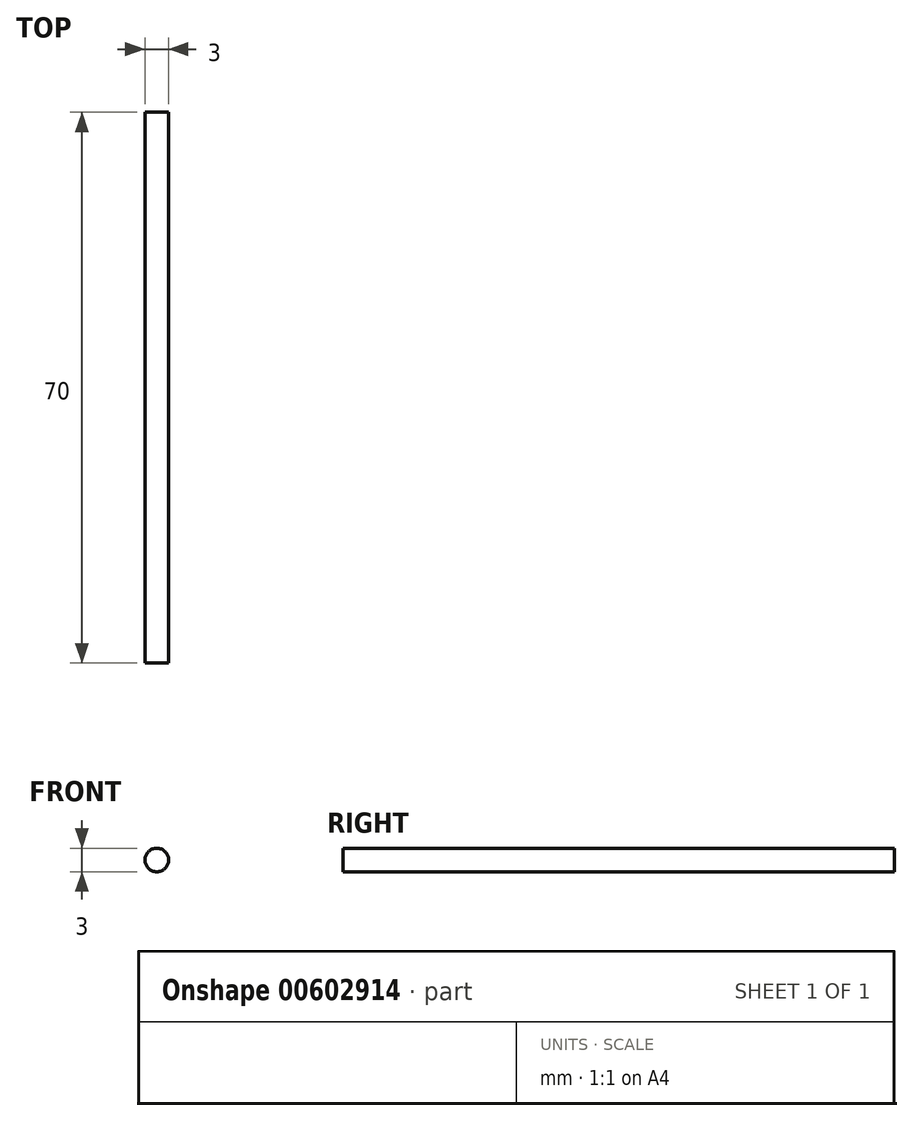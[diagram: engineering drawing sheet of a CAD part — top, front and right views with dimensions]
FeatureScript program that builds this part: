
annotation { "Feature Type Name" : "Feature", "Feature Type Description" : "" }
export const myFeature = defineFeature(function(context is Context, id is Id, definition is map)
    precondition{}
    {
        {
            var Q0;
            Q0=qCreatedBy(makeId("Front.planeOp"),FACE);
            var sketch = newSketch(context, id + "F0", { "sketchPlane" : qUnion([Q0])});
            skCircle(sketch, "E0", {"center": v(19.62, 11.85) * mm, "radius": 1.5 * mm});
            skSolve(sketch);
        }
        {
            var Q0;
            Q0=makeQuery(id+"F0.imprint","IMPRINT",FACE,{"disambiguationData":[TD([[makeQuery(id+"F0.imprint","IMPRINT",EDGE,{"derivedFrom":sQuery(id+"F0.wireOp",EDGE,"E0")}),1.0]])]});
            extrude(context, id + "F1", {"entities" : qUnion([Q0]), "depth" : 70 * mm, "offsetDistance" : 25 * mm});
        }
    });
